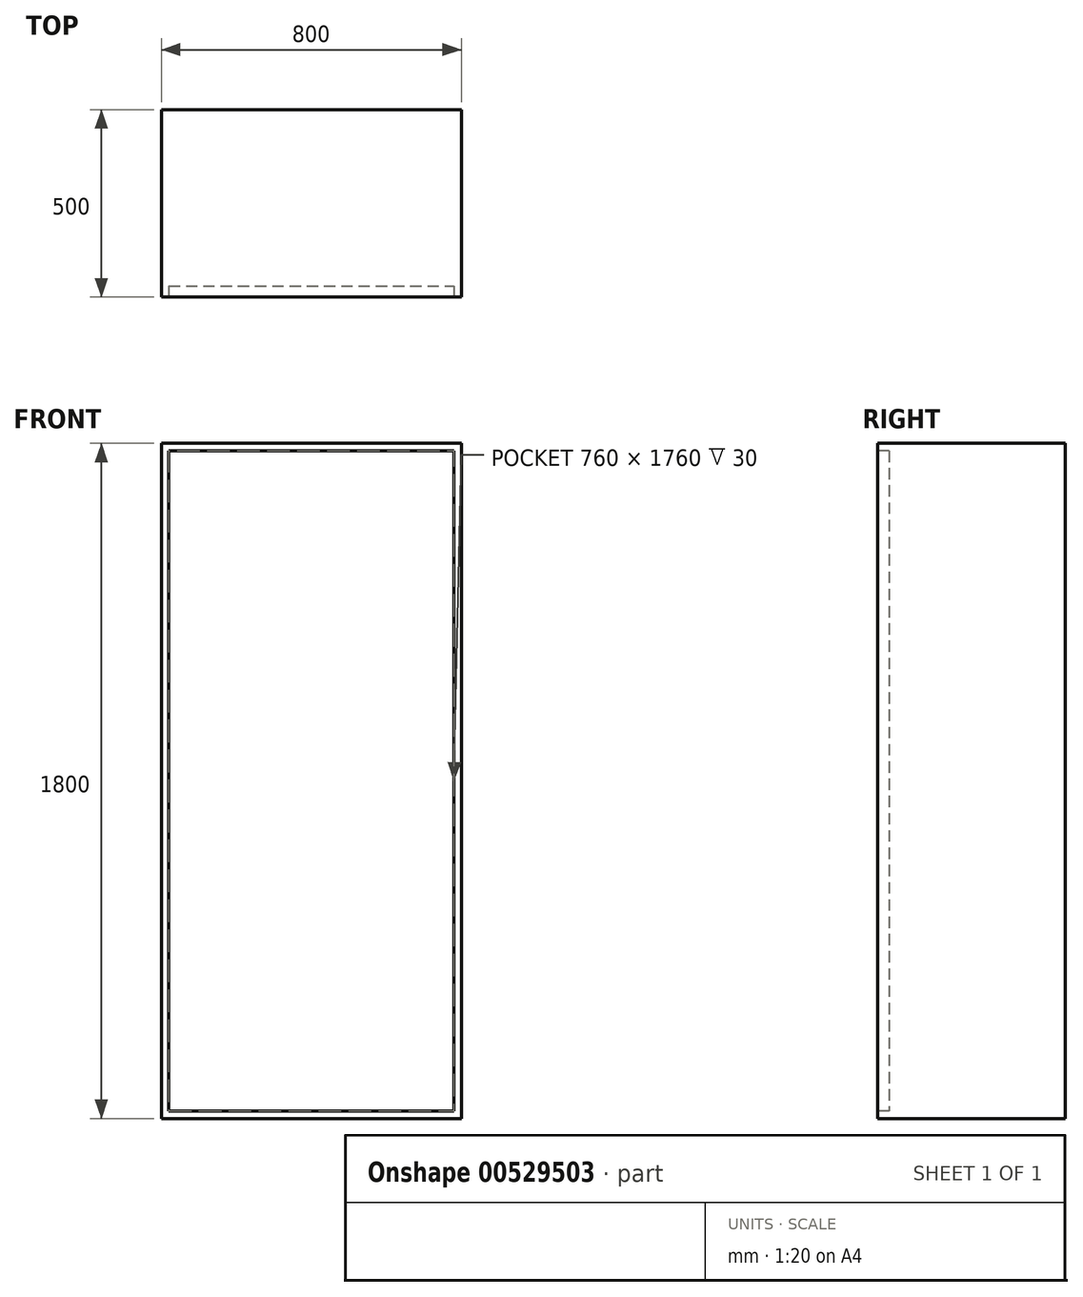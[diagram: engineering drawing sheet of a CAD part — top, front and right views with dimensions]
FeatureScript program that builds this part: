
annotation { "Feature Type Name" : "Feature", "Feature Type Description" : "" }
export const myFeature = defineFeature(function(context is Context, id is Id, definition is map)
    precondition{}
    {
        {
            var Q0;
            Q0=qCreatedBy(makeId("Top.planeOp"),FACE);
            var sketch = newSketch(context, id + "F0", { "sketchPlane" : qUnion([Q0])});
            skLineSegment(sketch, "E0.bottom", {"start": v(0, 0) * mm, "end": v(800, 0) * mm});
            skLineSegment(sketch, "E0.top", {"start": v(0, 500) * mm, "end": v(800, 500) * mm});
            skLineSegment(sketch, "E0.left", {"start": v(0, 0) * mm, "end": v(0, 500) * mm});
            skLineSegment(sketch, "E0.right", {"start": v(800, 0) * mm, "end": v(800, 500) * mm});
            skSolve(sketch);
        }
        {
            var Q0;
            Q0=makeQuery(id+"F0.imprint","IMPRINT",FACE,{"disambiguationData":[TD([[makeQuery(id+"F0.imprint","IMPRINT",EDGE,{"derivedFrom":sQuery(id+"F0.wireOp",EDGE,"E0.bottom")}),1.0]])]});
            extrude(context, id + "F1", {"entities" : qUnion([Q0]), "depth" : 1800 * mm, "offsetDistance" : 25 * mm});
        }
        {
            var Q0;
            Q0=makeQuery(id+"F1.opExtrude","SWEPT_FACE",FACE,{"disambiguationData":[OSD([sQuery(id+"F0.wireOp",EDGE,"E0.bottom")])]});
            var sketch = newSketch(context, id + "F2", { "sketchPlane" : qUnion([Q0])});
            skLineSegment(sketch, "E1.0", {"start": v(20, 20) * mm, "end": v(780, 20) * mm});
            skLineSegment(sketch, "E1.1", {"start": v(20, 1780) * mm, "end": v(20, 20) * mm});
            skLineSegment(sketch, "E1.2", {"start": v(780, 1780) * mm, "end": v(20, 1780) * mm});
            skLineSegment(sketch, "E1.3", {"start": v(780, 20) * mm, "end": v(780, 1780) * mm});
            skLineSegment(sketch, "E2.0", {"start": v(-5, -5) * mm, "end": v(805, -5) * mm});
            skLineSegment(sketch, "E2.1", {"start": v(-5, 1805) * mm, "end": v(-5, -5) * mm});
            skLineSegment(sketch, "E2.2", {"start": v(805, 1805) * mm, "end": v(-5, 1805) * mm});
            skLineSegment(sketch, "E2.3", {"start": v(805, -5) * mm, "end": v(805, 1805) * mm});
            skSolve(sketch);
        }
        {
            var Q0;
            Q0=makeQuery(id+"F2.imprint","IMPRINT",FACE,{"disambiguationData":[TD([[makeQuery(id+"F2.imprint","IMPRINT",EDGE,{"derivedFrom":sQuery(id+"F2.wireOp",EDGE,"E1.0")}),1.0]])]});
            extrude(context, id + "F3", {"entities" : qUnion([Q0]), "operationType" : NewBodyOperationType.REMOVE, "oppositeDirection" : true, "depth" : 30 * mm});
        }
    });
